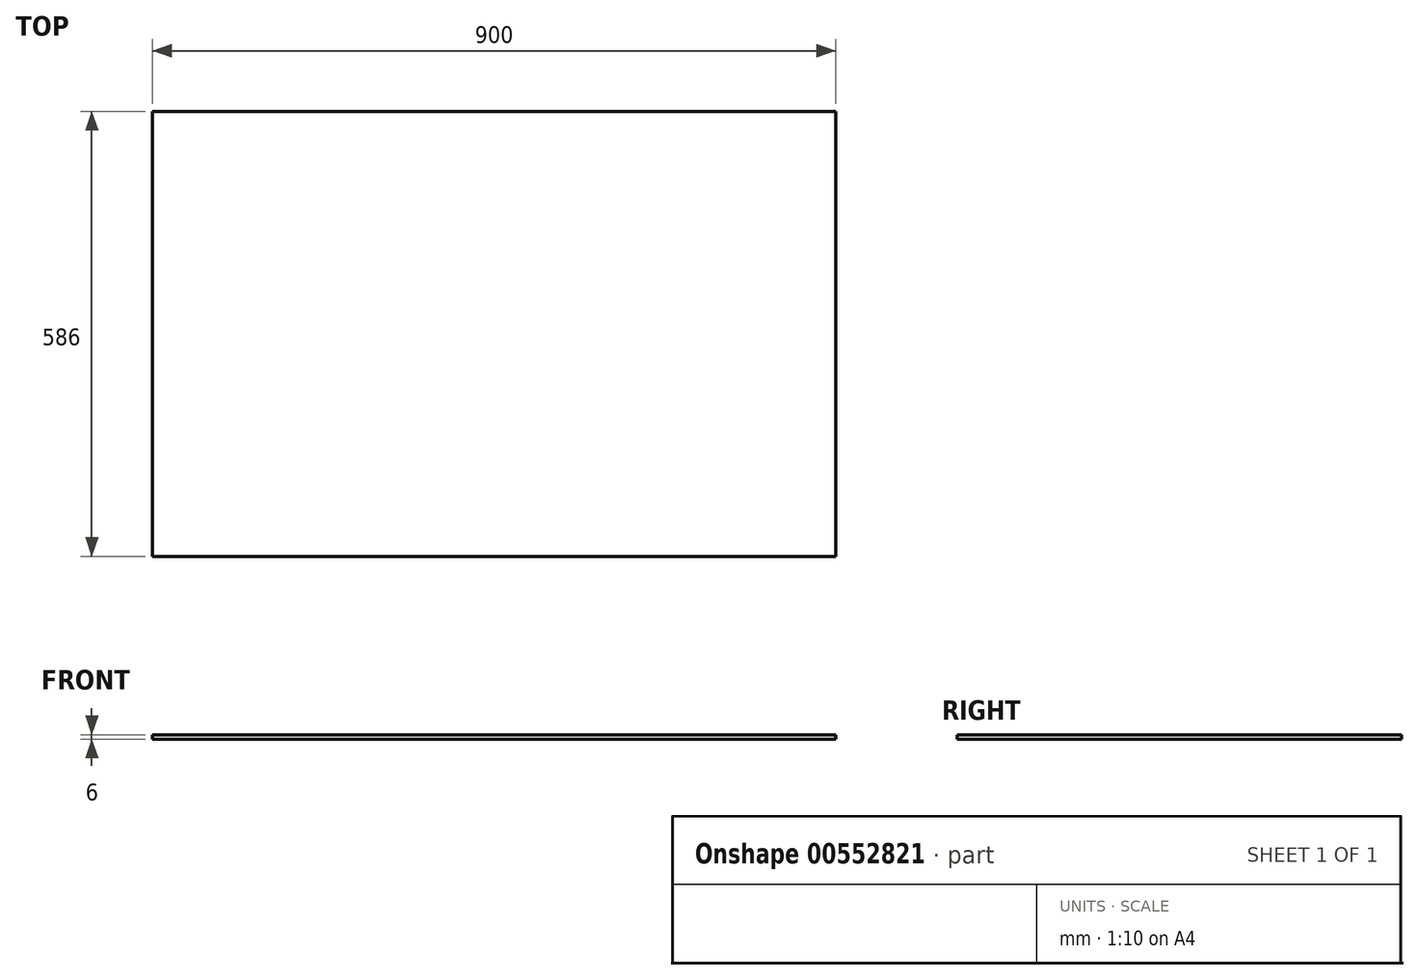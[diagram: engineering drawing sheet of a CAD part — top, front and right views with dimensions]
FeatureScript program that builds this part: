
annotation { "Feature Type Name" : "Feature", "Feature Type Description" : "" }
export const myFeature = defineFeature(function(context is Context, id is Id, definition is map)
    precondition{}
    {
        {
            var Q0;
            Q0=qCreatedBy(makeId("Top.planeOp"),FACE);
            var sketch = newSketch(context, id + "F0", { "sketchPlane" : qUnion([Q0])});
            skLineSegment(sketch, "E0.bottom", {"start": v(0, 0) * mm, "end": v(900, 0) * mm});
            skLineSegment(sketch, "E0.top", {"start": v(0, 586) * mm, "end": v(900, 586) * mm});
            skLineSegment(sketch, "E0.left", {"start": v(0, 0) * mm, "end": v(0, 586) * mm});
            skLineSegment(sketch, "E0.right", {"start": v(900, 0) * mm, "end": v(900, 586) * mm});
            skSolve(sketch);
        }
        {
            var Q0;
            Q0=makeQuery(id+"F0.imprint","IMPRINT",FACE,{"disambiguationData":[TD([[makeQuery(id+"F0.imprint","IMPRINT",EDGE,{"derivedFrom":sQuery(id+"F0.wireOp",EDGE,"E0.bottom")}),1.0]])]});
            extrude(context, id + "F1", {"entities" : qUnion([Q0]), "depth" : 6 * mm, "offsetDistance" : 25 * mm});
        }
    });
